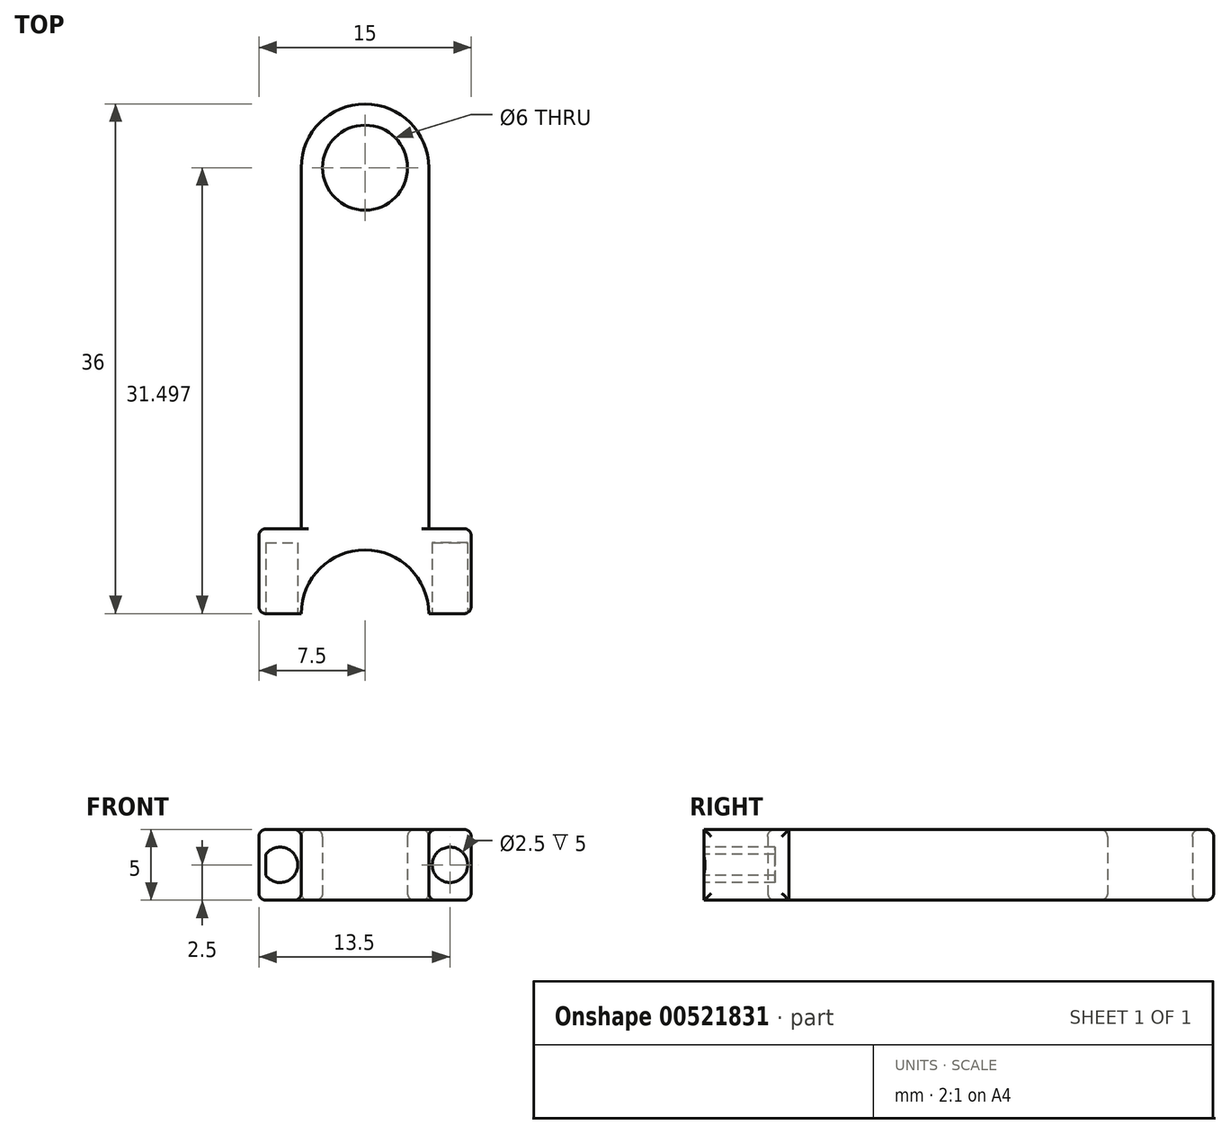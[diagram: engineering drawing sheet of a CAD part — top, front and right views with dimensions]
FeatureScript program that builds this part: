
annotation { "Feature Type Name" : "Feature", "Feature Type Description" : "" }
export const myFeature = defineFeature(function(context is Context, id is Id, definition is map)
    precondition{}
    {
        {
            var Q0;
            Q0=qCreatedBy(makeId("Top.planeOp"),FACE);
            var sketch = newSketch(context, id + "F0", { "sketchPlane" : qUnion([Q0])});
            skLineSegment(sketch, "E0", {"start": v(-4.5, 15.18) * mm, "end": v(4.5, 15.18) * mm});
            skLineSegment(sketch, "E1", {"start": v(7.5, -14.82) * mm, "end": v(-7.5, -14.82) * mm});
            skPoint(sketch, "E2", {"position": v(0, 15.18) * mm});
            skPoint(sketch, "E3", {"position": v(0, -20.82) * mm});
            skCircle(sketch, "E4", {"center": v(0, -20.82) * mm, "radius": 4.5 * mm});
            skLineSegment(sketch, "E5", {"start": v(0, 15.18) * mm, "end": v(0, 10.68) * mm});
            skCircle(sketch, "E6", {"center": v(0, 10.68) * mm, "radius": 3 * mm});
            skLineSegment(sketch, "E7.top", {"start": v(7.5, -20.82) * mm, "end": v(-7.5, -20.82) * mm});
            skLineSegment(sketch, "E7.left", {"start": v(7.5, -14.82) * mm, "end": v(7.5, -20.82) * mm});
            skLineSegment(sketch, "E7.right", {"start": v(-7.5, -14.82) * mm, "end": v(-7.5, -20.82) * mm});
            skLineSegment(sketch, "E8", {"start": v(-4.5, 15.18) * mm, "end": v(-4.5, -14.82) * mm});
            skLineSegment(sketch, "E9", {"start": v(4.5, 15.18) * mm, "end": v(4.5, -14.82) * mm});
            skSolve(sketch);
        }
        {
            var Q0;
            {var subQ1=sQuery(id+"F0.wireOp",EDGE,"om51KBJW-K96v-Nftr-g2KN-rlsTVNBrCXjp");Q0=makeQuery(id+"F0.imprint","IMPRINT",FACE,{"disambiguationData":[TD([[makeQuery(id+"F0.imprint","IMPRINT",EDGE,{"derivedFrom":subQ1}),-1.0]])]});}
            var Q1;
            {var subQ5=sQuery(id+"F0.wireOp",EDGE,"E7.left");Q1=makeQuery(id+"F0.imprint","IMPRINT",FACE,{"disambiguationData":[TD([[makeQuery(id+"F0.imprint","IMPRINT",EDGE,{"derivedFrom":subQ5}),-1.0]])]});}
            var Q2;
            {var subQ5=sQuery(id+"F0.wireOp",EDGE,"E7.right");Q2=makeQuery(id+"F0.imprint","IMPRINT",FACE,{"disambiguationData":[TD([[makeQuery(id+"F0.imprint","IMPRINT",EDGE,{"derivedFrom":subQ5}),1.0]])]});}
            var Q3;
            Q3=makeQuery(id+"F0.imprint","IMPRINT",FACE,{"disambiguationData":[TD([[makeQuery(id+"F0.imprint","IMPRINT",EDGE,{"derivedFrom":sQuery(id+"F0.wireOp",EDGE,"E6")}),-1.0]])]});
            extrude(context, id + "F1", {"entities" : qUnion([Q0, Q1, Q2, Q3]), "depth" : 5 * mm, "offsetDistance" : 25 * mm});
        }
        {
            var Q0;
            Q0=makeQuery(id+"F1.opExtrude","SWEPT_EDGE",EDGE,{"disambiguationData":[OSD([sQuery(id+"F0.wireOp",EDGE,"E0"),sQuery(id+"F0.wireOp",EDGE,"KS9etzK5-rIq5-qhlt-kS3d-AAEQj4MSfW2m")])]});
            var Q1;
            Q1=makeQuery(id+"F1.opExtrude","SWEPT_EDGE",EDGE,{"disambiguationData":[OSD([sQuery(id+"F0.wireOp",EDGE,"E0"),sQuery(id+"F0.wireOp",EDGE,"om51KBJW-K96v-Nftr-g2KN-rlsTVNBrCXjp")])]});
            fillet(context, id + "F2", {"entities" : qUnion([Q0, Q1]), "radius" : 4.5 * mm, "tangentPropagation" : true, "allowEdgeOverflow" : false});
        }
        {
            var Q0;
            Q0=makeQuery(id+"F1.opExtrude","CAP_EDGE",EDGE,{"disambiguationData":[OSD([sQuery(id+"F0.wireOp",EDGE,"E8")])],"isStart":false});
            var Q1;
            Q1=makeQuery(id+"F1.opExtrude","CAP_EDGE",EDGE,{"disambiguationData":[OSD([sQuery(id+"F0.wireOp",EDGE,"E8")])],"isStart":true});
            var Q2;
            {var subQ0=sQuery(id+"F0.wireOp",EDGE,"E1");Q2=makeQuery(id+"F1.opExtrude","CAP_EDGE",EDGE,{"disambiguationData":[OSD([subQ0]),TDD([makeQuery(id+"F0.imprint","IMPRINT",EDGE,{"disambiguationData":[TD([[makeQuery(id+"F0.imprint","INTERSECT",VERTEX,{"derivedFrom":[subQ0,sQuery(id+"F0.wireOp",EDGE,"E7.right")]}),1.0]])],"derivedFrom":subQ0})])],"isStart":false});}
            var Q3;
            {var subQ0=sQuery(id+"F0.wireOp",EDGE,"E1");Q3=makeQuery(id+"F1.opExtrude","CAP_EDGE",EDGE,{"disambiguationData":[OSD([subQ0]),TDD([makeQuery(id+"F0.imprint","IMPRINT",EDGE,{"disambiguationData":[TD([[makeQuery(id+"F0.imprint","INTERSECT",VERTEX,{"derivedFrom":[subQ0,sQuery(id+"F0.wireOp",EDGE,"E7.right")]}),1.0]])],"derivedFrom":subQ0})])],"isStart":true});}
            var Q4;
            Q4=makeQuery(id+"F1.opExtrude","SWEPT_EDGE",EDGE,{"disambiguationData":[OSD([sQuery(id+"F0.wireOp",EDGE,"E1"),sQuery(id+"F0.wireOp",EDGE,"E7.right")])]});
            var Q5;
            Q5=makeQuery(id+"F1.opExtrude","SWEPT_EDGE",EDGE,{"disambiguationData":[OSD([sQuery(id+"F0.wireOp",EDGE,"E1"),sQuery(id+"F0.wireOp",EDGE,"E7.left")])]});
            var Q6;
            {var subQ0=sQuery(id+"F0.wireOp",EDGE,"E1");Q6=makeQuery(id+"F1.opExtrude","CAP_EDGE",EDGE,{"disambiguationData":[OSD([subQ0]),TDD([makeQuery(id+"F0.imprint","IMPRINT",EDGE,{"disambiguationData":[TD([[makeQuery(id+"F0.imprint","INTERSECT",VERTEX,{"derivedFrom":[subQ0,sQuery(id+"F0.wireOp",EDGE,"E7.left")]}),-1.0]])],"derivedFrom":subQ0})])],"isStart":true});}
            var Q7;
            {var subQ0=sQuery(id+"F0.wireOp",EDGE,"E1");Q7=makeQuery(id+"F1.opExtrude","CAP_EDGE",EDGE,{"disambiguationData":[OSD([subQ0]),TDD([makeQuery(id+"F0.imprint","IMPRINT",EDGE,{"disambiguationData":[TD([[makeQuery(id+"F0.imprint","INTERSECT",VERTEX,{"derivedFrom":[subQ0,sQuery(id+"F0.wireOp",EDGE,"E7.left")]}),-1.0]])],"derivedFrom":subQ0})])],"isStart":false});}
            var Q8;
            Q8=makeQuery(id+"F1.opExtrude","CAP_EDGE",EDGE,{"disambiguationData":[OSD([sQuery(id+"F0.wireOp",EDGE,"E7.right")])],"isStart":true});
            var Q9;
            Q9=makeQuery(id+"F1.opExtrude","CAP_EDGE",EDGE,{"disambiguationData":[OSD([sQuery(id+"F0.wireOp",EDGE,"E7.right")])],"isStart":false});
            var Q10;
            Q10=makeQuery(id+"F1.opExtrude","CAP_EDGE",EDGE,{"disambiguationData":[OSD([sQuery(id+"F0.wireOp",EDGE,"E7.left")])],"isStart":false});
            var Q11;
            Q11=makeQuery(id+"F1.opExtrude","CAP_EDGE",EDGE,{"disambiguationData":[OSD([sQuery(id+"F0.wireOp",EDGE,"E7.left")])],"isStart":true});
            var Q12;
            Q12=makeQuery(id+"F1.opExtrude","CAP_EDGE",EDGE,{"disambiguationData":[OSD([sQuery(id+"F0.wireOp",EDGE,"E6")])],"isStart":false});
            var Q13;
            Q13=makeQuery(id+"F1.opExtrude","CAP_EDGE",EDGE,{"disambiguationData":[OSD([sQuery(id+"F0.wireOp",EDGE,"E6")])],"isStart":true});
            var Q14;
            Q14=makeQuery(id+"F1.opExtrude","CAP_EDGE",EDGE,{"disambiguationData":[OSD([sQuery(id+"F0.wireOp",EDGE,"E4")])],"isStart":false});
            var Q15;
            Q15=makeQuery(id+"F1.opExtrude","CAP_EDGE",EDGE,{"disambiguationData":[OSD([sQuery(id+"F0.wireOp",EDGE,"E4")])],"isStart":true});
            fillet(context, id + "F3", {"entities" : qUnion([Q0, Q1, Q2, Q3, Q4, Q5, Q6, Q7, Q8, Q9, Q10, Q11, Q12, Q13, Q14, Q15]), "radius" : .5 * mm, "tangentPropagation" : true, "allowEdgeOverflow" : false});
        }
        {
            var Q0;
            {var subQ0=sQuery(id+"F0.wireOp",EDGE,"E7.top");Q0=makeQuery(id+"F1.opExtrude","SWEPT_FACE",FACE,{"disambiguationData":[OSD([subQ0]),TDD([makeQuery(id+"F0.imprint","IMPRINT",EDGE,{"disambiguationData":[TD([[makeQuery(id+"F0.imprint","INTERSECT",VERTEX,{"derivedFrom":[subQ0,sQuery(id+"F0.wireOp",EDGE,"E7.right")]}),1.0]])],"derivedFrom":subQ0})])]});}
            var sketch = newSketch(context, id + "F4", { "sketchPlane" : qUnion([Q0])});
            skLineSegment(sketch, "E10.bottom", {"start": v(-4.5, 5) * mm, "end": v(-6, 5) * mm});
            skLineSegment(sketch, "E10.top", {"start": v(-4.5, 2.5) * mm, "end": v(-6, 2.5) * mm});
            skLineSegment(sketch, "E10.left", {"start": v(-4.5, 5) * mm, "end": v(-4.5, 2.5) * mm});
            skLineSegment(sketch, "E10.right", {"start": v(-6, 5) * mm, "end": v(-6, 2.5) * mm});
            skLineSegment(sketch, "E11", {"start": v(-4.5, 5) * mm, "end": v(4.5, 5) * mm});
            skLineSegment(sketch, "E12.bottom", {"start": v(4.5, 5) * mm, "end": v(6, 5) * mm});
            skLineSegment(sketch, "E12.top", {"start": v(4.5, 2.5) * mm, "end": v(6, 2.5) * mm});
            skLineSegment(sketch, "E12.left", {"start": v(4.5, 5) * mm, "end": v(4.5, 2.5) * mm});
            skLineSegment(sketch, "E12.right", {"start": v(6, 5) * mm, "end": v(6, 2.5) * mm});
            skCircle(sketch, "E13", {"center": v(-6, 2.5) * mm, "radius": 1.25 * mm});
            skCircle(sketch, "E14", {"center": v(6, 2.5) * mm, "radius": 1.25 * mm});
            skSolve(sketch);
        }
        {
            var Q0;
            {var subQ0=sQuery(id+"F4.wireOp",EDGE,"E12.right");var subQ1=sQuery(id+"F4.wireOp",EDGE,"E12.top");var subQ2=makeQuery(id+"F4.imprint","INTERSECT",VERTEX,{"derivedFrom":[subQ1,subQ0]});Q0=makeQuery(id+"F4.imprint","IMPRINT",FACE,{"disambiguationData":[TD([[makeQuery(id+"F4.imprint","IMPRINT",EDGE,{"disambiguationData":[TD([[subQ2,1.0]])],"derivedFrom":subQ1}),-1.0]])]});}
            var Q1;
            {var subQ0=sQuery(id+"F4.wireOp",EDGE,"E12.right");var subQ1=sQuery(id+"F4.wireOp",EDGE,"E12.top");var subQ2=makeQuery(id+"F4.imprint","INTERSECT",VERTEX,{"derivedFrom":[subQ1,subQ0]});Q1=makeQuery(id+"F4.imprint","IMPRINT",FACE,{"disambiguationData":[TD([[makeQuery(id+"F4.imprint","IMPRINT",EDGE,{"disambiguationData":[TD([[subQ2,1.0]])],"derivedFrom":subQ1}),1.0]])]});}
            var Q2;
            {var subQ0=sQuery(id+"F4.wireOp",EDGE,"E10.right");var subQ1=sQuery(id+"F4.wireOp",EDGE,"E10.top");var subQ2=makeQuery(id+"F4.imprint","INTERSECT",VERTEX,{"derivedFrom":[subQ1,subQ0]});Q2=makeQuery(id+"F4.imprint","IMPRINT",FACE,{"disambiguationData":[TD([[makeQuery(id+"F4.imprint","IMPRINT",EDGE,{"disambiguationData":[TD([[subQ2,1.0]])],"derivedFrom":subQ1}),1.0]])]});}
            var Q3;
            {var subQ0=sQuery(id+"F4.wireOp",EDGE,"E10.right");var subQ1=sQuery(id+"F4.wireOp",EDGE,"E10.top");var subQ2=makeQuery(id+"F4.imprint","INTERSECT",VERTEX,{"derivedFrom":[subQ1,subQ0]});Q3=makeQuery(id+"F4.imprint","IMPRINT",FACE,{"disambiguationData":[TD([[makeQuery(id+"F4.imprint","IMPRINT",EDGE,{"disambiguationData":[TD([[subQ2,1.0]])],"derivedFrom":subQ1}),-1.0]])]});}
            extrude(context, id + "F5", {"entities" : qUnion([Q0, Q1, Q2, Q3]), "operationType" : NewBodyOperationType.REMOVE, "oppositeDirection" : true, "depth" : 5 * mm, "offsetDistance" : 25 * mm});
        }
    });
